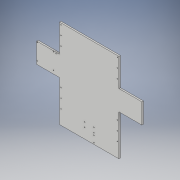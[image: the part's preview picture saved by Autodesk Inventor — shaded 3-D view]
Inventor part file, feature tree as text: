
AUTODESK INVENTOR PART (.ipt)
format: ipt  version: 2019 (Build 230136000, 136)  size: 226,304 bytes
history: native  units: in
note: dims shown in document units (in); Inventor stores cm internally (conversion verified against a paired STEP export)
features: extrude x5, sketch x5, plane x2
ambient origin geometry x8: Origin, YZ Plane, XZ Plane, XY Plane, X Axis, Y Axis, Z Axis, Center Point
bodies: Solid1 (feature_tree)
feature tree (12):
  plane  "Work Plane32"
  extrude  "Extrusion20"  Depth=0.25in TaperAngle=0.0deg
  plane  "Work Plane28"
  extrude  "Extrusion21"  Depth=3.25in
  extrude  "Extrusion22"  Depth=0.2in
  extrude  "Extrusion23"  Depth=0.2in
  extrude  "Extrusion24"  Depth=0.25in
  sketch  "Sketch36"  dims[d408=0.25in d409=0.0in d410=0.25in d411=0.0in]
  sketch  "Sketch38"  dims[d412=3.25in d413=10.0in]
  sketch  "Sketch39"  dims[d414=1.25in d415=0.2in]
  sketch  "Sketch40"  dims[d416=0.2in d417=0.2in]
  sketch  "Sketch41"  dims[d418=0.25in d419=0.0in d420=0.25in d421=0.25in d422=1.5in d423=1.5in d424=0.25in d425=0.25in d426=1.5in d427=1.5in d428=2.3in d429=1.5in d430=1.5in d431=0.25in d432=0.25in d433=0.25in d434=0.14in d435=0.14in d436=0.14in d437=0.14in d438=0.14in d439=0.14in d440=0.14in d441=0.14in d442=0.14in d443=0.14in d444=0.14in d445=0.14in d446=0.25in d447=0.0in d448=1.45in d449=0.25in d450=0.0in d284=1.0in d285=1.0in]
